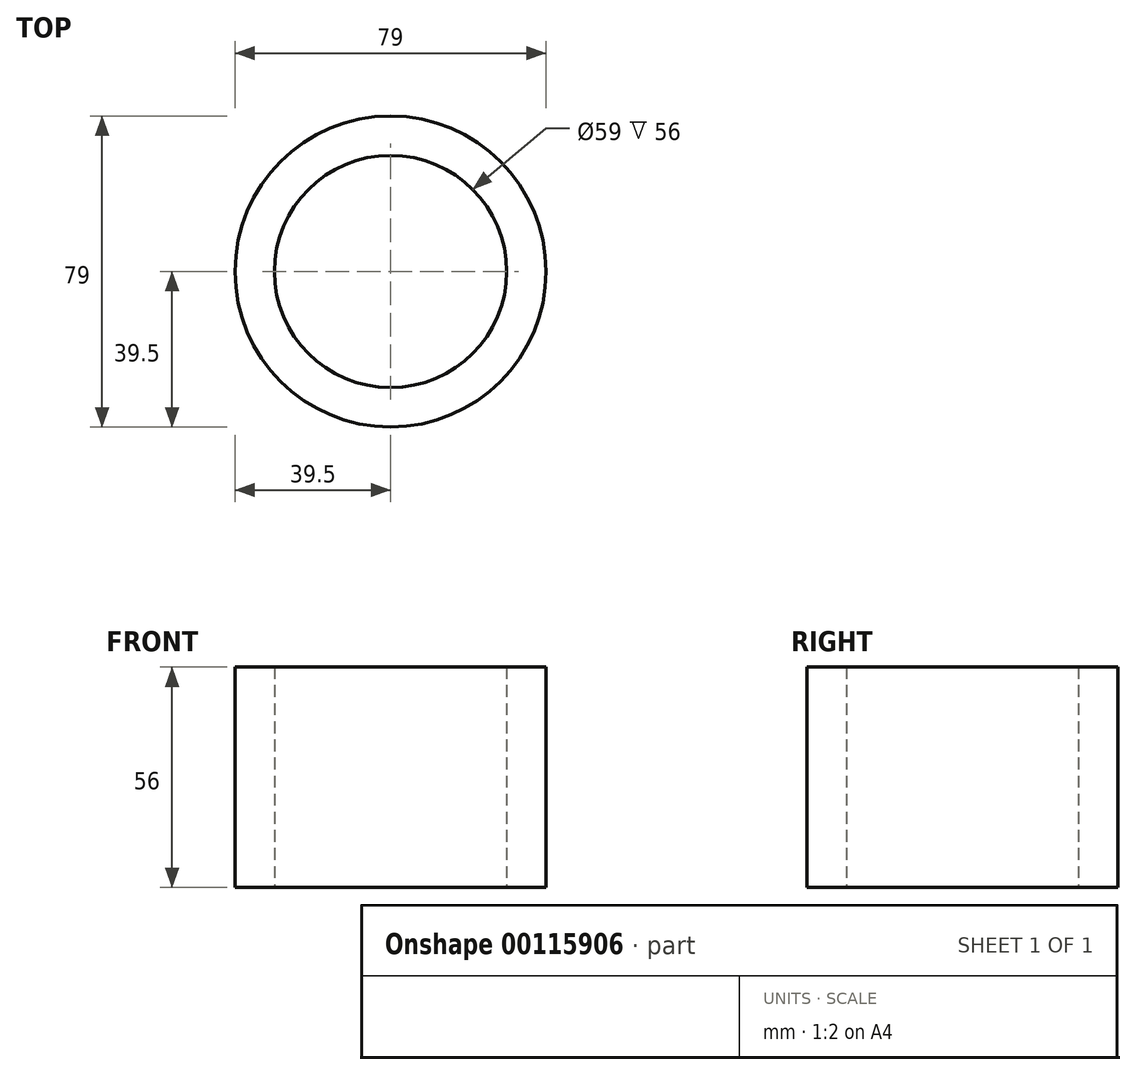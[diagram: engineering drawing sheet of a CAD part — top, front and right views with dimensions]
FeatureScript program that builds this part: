
annotation { "Feature Type Name" : "Feature", "Feature Type Description" : "" }
export const myFeature = defineFeature(function(context is Context, id is Id, definition is map)
    precondition{}
    {
        {
            var Q0;
            Q0=qCreatedBy(makeId("Top.planeOp"),FACE);
            var sketch = newSketch(context, id + "F0", { "sketchPlane" : qUnion([Q0])});
            skCircle(sketch, "E0", {"center": v(0, 0) * mm, "radius": 39.5 * mm});
            skCircle(sketch, "E1", {"center": v(0, 0) * mm, "radius": 29.5 * mm});
            skSolve(sketch);
        }
        {
            var Q0;
            Q0=qSketchRegion(id+"F0",true);
            extrude(context, id + "F1", {"entities" : qUnion([Q0]), "depth" : 56 * mm});
        }
    });
